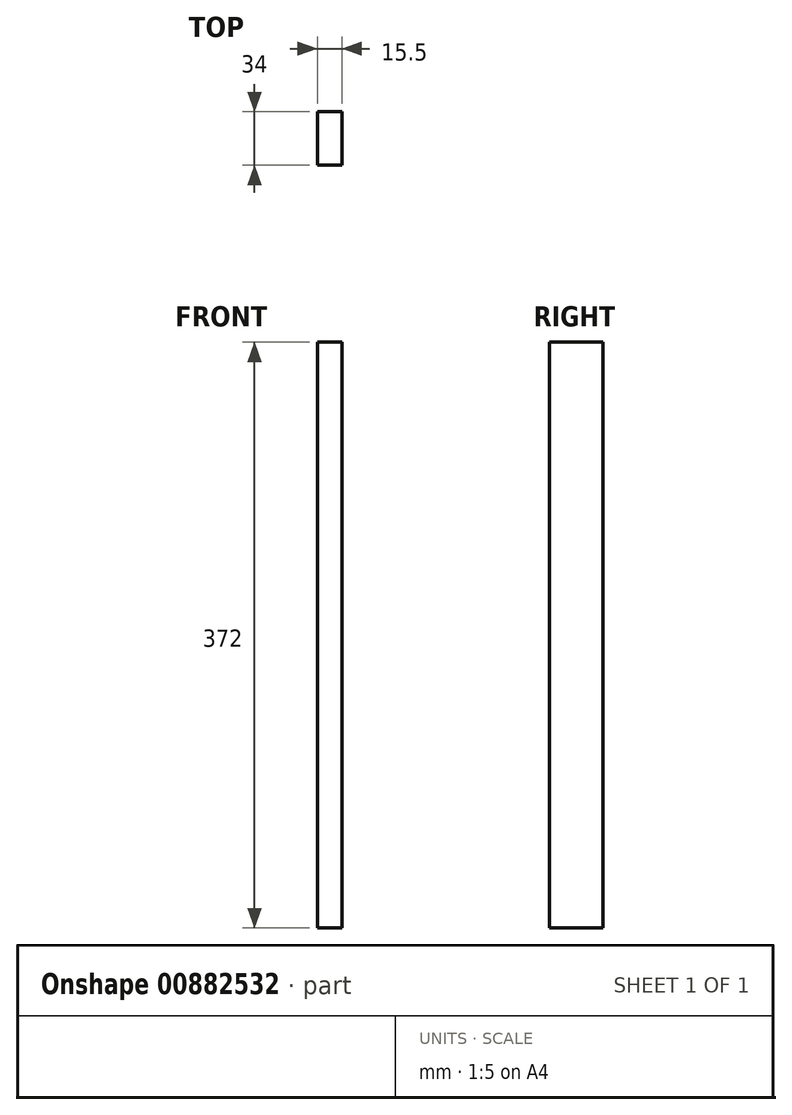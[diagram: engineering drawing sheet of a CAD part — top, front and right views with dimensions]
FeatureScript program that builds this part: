
annotation { "Feature Type Name" : "Feature", "Feature Type Description" : "" }
export const myFeature = defineFeature(function(context is Context, id is Id, definition is map)
    precondition{}
    {
        {
            var Q0;
            Q0=qCreatedBy(makeId("Top.planeOp"),FACE);
            var sketch = newSketch(context, id + "F0", { "sketchPlane" : qUnion([Q0])});
            skLineSegment(sketch, "E0.bottom", {"start": v(0, 0) * mm, "end": v(15.5, 0) * mm});
            skLineSegment(sketch, "E0.top", {"start": v(0, -34) * mm, "end": v(15.5, -34) * mm});
            skLineSegment(sketch, "E0.left", {"start": v(0, 0) * mm, "end": v(0, -34) * mm});
            skLineSegment(sketch, "E0.right", {"start": v(15.5, 0) * mm, "end": v(15.5, -34) * mm});
            skSolve(sketch);
        }
        {
            var Q0;
            Q0 = qSketchRegion(id + "F0", true);
            extrude(context, id + "F1", {"entities" : qUnion([Q0]), "depth" : 372 * mm, "offsetDistance" : 25 * mm});
        }
    });
